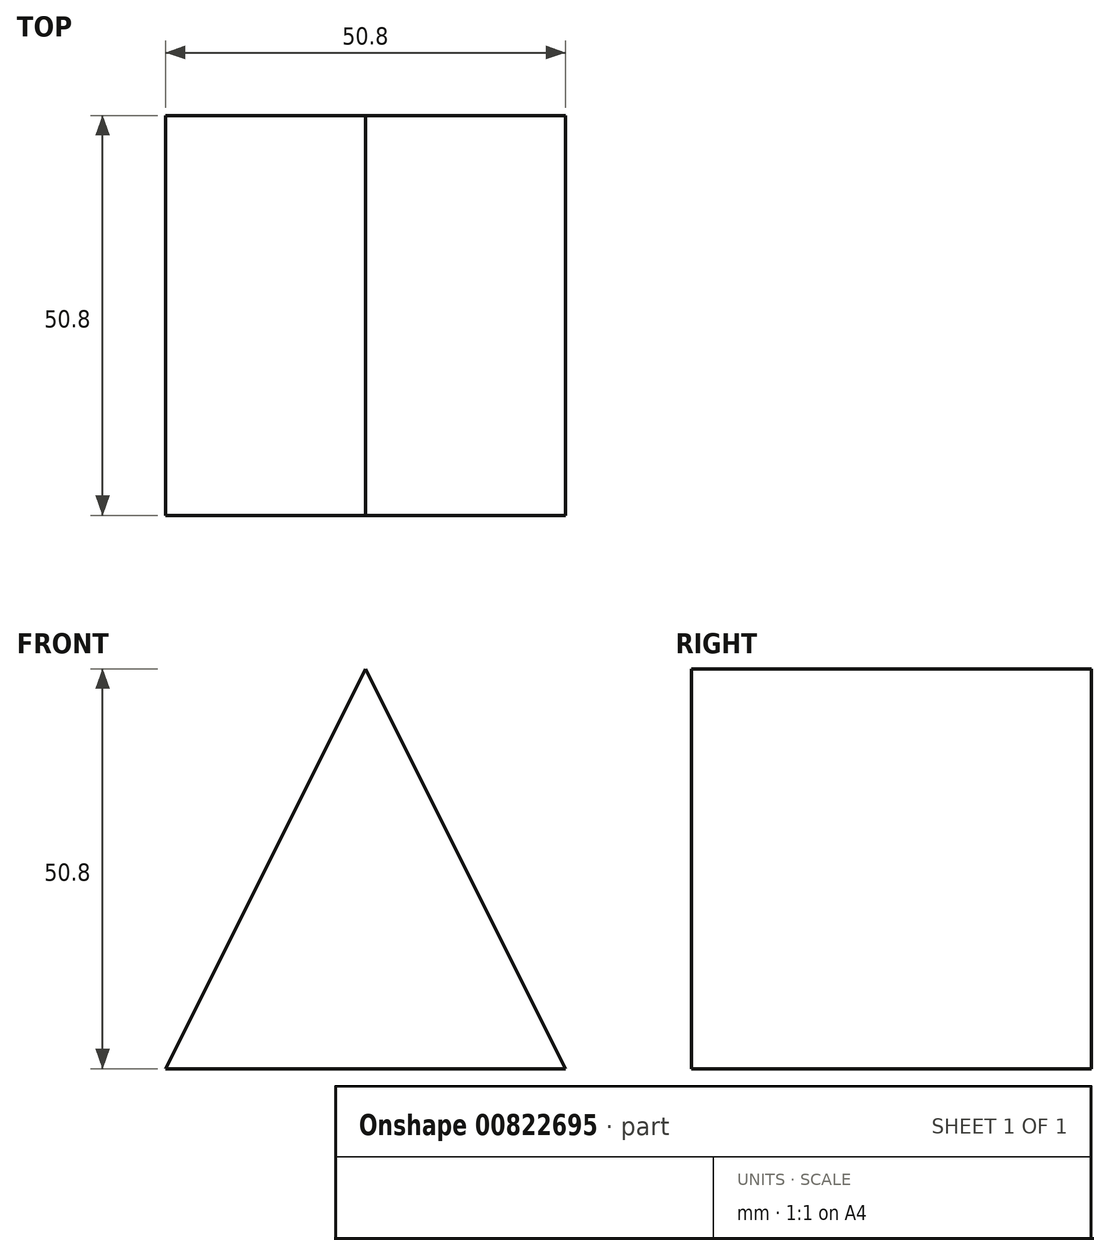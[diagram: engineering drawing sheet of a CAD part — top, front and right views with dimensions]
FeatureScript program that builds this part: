
annotation { "Feature Type Name" : "Feature", "Feature Type Description" : "" }
export const myFeature = defineFeature(function(context is Context, id is Id, definition is map)
    precondition{}
    {
        {
            var Q0;
            Q0=qCreatedBy(makeId("Top.planeOp"),FACE);
            var sketch = newSketch(context, id + "F0", { "sketchPlane" : qUnion([Q0])});
            skLineSegment(sketch, "E0.bottom", {"start": v(25.4, -25.4) * mm, "end": v(-25.4, -25.4) * mm});
            skLineSegment(sketch, "E0.top", {"start": v(25.4, 25.4) * mm, "end": v(-25.4, 25.4) * mm});
            skLineSegment(sketch, "E0.left", {"start": v(25.4, -25.4) * mm, "end": v(25.4, 25.4) * mm});
            skLineSegment(sketch, "E0.right", {"start": v(-25.4, -25.4) * mm, "end": v(-25.4, 25.4) * mm});
            skPoint(sketch, "E0.middle", {"position": v(0, 0) * mm});
            skSolve(sketch);
        }
        {
            var Q0;
            Q0=makeQuery(id+"F0.imprint","IMPRINT",FACE,{"disambiguationData":[TD([[makeQuery(id+"F0.imprint","IMPRINT",EDGE,{"derivedFrom":sQuery(id+"F0.wireOp",EDGE,"E0.bottom")}),-1.0]])]});
            extrude(context, id + "F1", {"entities" : qUnion([Q0]), "depth" : 50.8 * mm, "offsetDistance" : 25.4 * mm});
        }
        {
            var Q0;
            Q0=makeQuery(id+"F1.opExtrude","SWEPT_FACE",FACE,{"disambiguationData":[OSD([sQuery(id+"F0.wireOp",EDGE,"E0.bottom")])]});
            var sketch = newSketch(context, id + "F2", { "sketchPlane" : qUnion([Q0])});
            skLineSegment(sketch, "E1", {"start": v(0, 50.8) * mm, "end": v(-25.4, 0) * mm});
            skSolve(sketch);
        }
        {
            var Q0;
            {var subQ0=sQuery(id+"F2.wireOp",EDGE,"E1");Q0=makeQuery(id+"F2.imprint","IMPRINT",FACE,{"disambiguationData":[TD([[makeQuery(id+"F2.imprint","IMPRINT",EDGE,{"derivedFrom":subQ0}),-1.0]])]});}
            extrude(context, id + "F3", {"entities" : qUnion([Q0]), "operationType" : NewBodyOperationType.REMOVE, "oppositeDirection" : true, "depth" : 76.2 * mm, "offsetDistance" : 25.4 * mm});
        }
        {
            var Q0;
            Q0=makeQuery(id+"F1.opExtrude","SWEPT_FACE",FACE,{"disambiguationData":[OSD([sQuery(id+"F0.wireOp",EDGE,"E0.bottom")])]});
            var sketch = newSketch(context, id + "F4", { "sketchPlane" : qUnion([Q0])});
            skLineSegment(sketch, "E2", {"start": v(0, 50.8) * mm, "end": v(25.4, 0) * mm});
            skSolve(sketch);
        }
        {
            var Q0;
            Q0 = qSketchRegion(id + "F4", true);
            var Q1;
            Q1=makeQuery(id+"F4.imprint","IMPRINT",FACE,{"disambiguationData":[TD([[makeQuery(id+"F4.imprint","IMPRINT",EDGE,{"derivedFrom":sQuery(id+"F4.wireOp",EDGE,"E2")}),1.0]])]});
            extrude(context, id + "F5", {"entities" : qUnion([Q0, Q1]), "operationType" : NewBodyOperationType.REMOVE, "oppositeDirection" : true, "depth" : 76.2 * mm, "offsetDistance" : 25.4 * mm});
        }
    });
